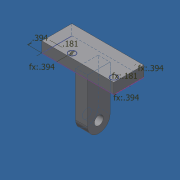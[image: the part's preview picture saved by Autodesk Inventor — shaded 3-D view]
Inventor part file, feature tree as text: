
AUTODESK INVENTOR PART (.ipt)
format: ipt  version: 2021 (Build 250183000, 183)  size: 111,616 bytes
history: native  units: in
note: dims shown in document units (in); Inventor stores cm internally (conversion verified against a paired STEP export)
features: extrude x3, sketch x3
ambient origin geometry x8: Origin, YZ Plane, XZ Plane, XY Plane, X Axis, Y Axis, Z Axis, Center Point
bodies: Solid1 (feature_tree)
feature tree (6):
  extrude  "Extrusion1"  Depth=0.5906in
  extrude  "Extrusion2"  Depth=0.315in TaperAngle=0.0deg
  extrude  "Extrusion3"  Depth=0.0984in
  sketch  "Sketch1"  dims[d0=0.2362in d1=0.5906in]
  sketch  "Sketch2"  dims[d2=1.7717in d3=0.315in d4=0.0in]
  sketch  "Sketch3"  dims[d5=0.7874in d6=0.0984in d7=0.0in d8=0.2756in d9=0.7874in d10=1.1024in d11=0.0in d12=0.0in d13=0.3937in d14=0.3937in d15=0.1811in d16=0.1811in d17=0.3937in d18=0.3937in d19=0.7874in d20=0.0in]
